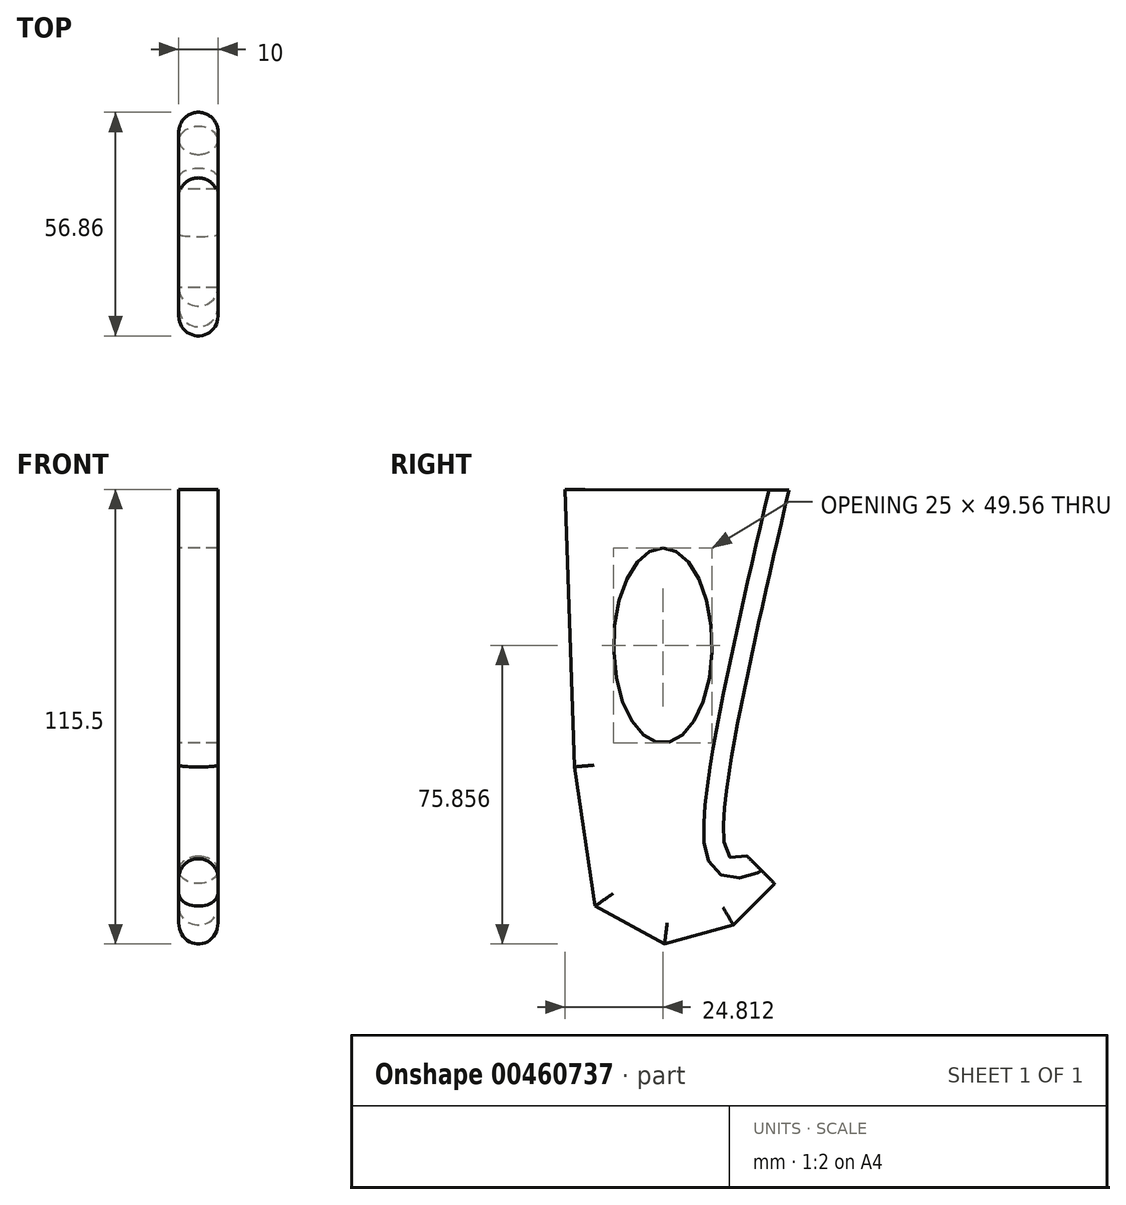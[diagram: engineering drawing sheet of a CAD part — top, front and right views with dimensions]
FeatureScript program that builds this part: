
annotation { "Feature Type Name" : "Feature", "Feature Type Description" : "" }
export const myFeature = defineFeature(function(context is Context, id is Id, definition is map)
    precondition{}
    {
        {
            var Q0;
            Q0=qCreatedBy(makeId("Top.planeOp"),FACE);
            var sketch = newSketch(context, id + "F0", { "sketchPlane" : qUnion([Q0])});
            skLineSegment(sketch, "E0.bottom", {"start": v(50, 50) * mm, "end": v(-50, 50) * mm});
            skLineSegment(sketch, "E0.top", {"start": v(50, -50) * mm, "end": v(-50, -50) * mm});
            skLineSegment(sketch, "E0.left", {"start": v(50, 50) * mm, "end": v(50, -50) * mm});
            skLineSegment(sketch, "E0.right", {"start": v(-50, 50) * mm, "end": v(-50, -50) * mm});
            skPoint(sketch, "E0.middle", {"position": v(0, 0) * mm});
            skSolve(sketch);
        }
        {
            var Q0;
            Q0=qCreatedBy(makeId("Right.planeOp"),FACE);
            var sketch = newSketch(context, id + "F1", { "sketchPlane" : qUnion([Q0])});
            skLineSegment(sketch, "E1", {"start": v(32.93, -92.93) * mm, "end": v(40, -100) * mm});
            skLineSegment(sketch, "E2", {"start": v(40, -100) * mm, "end": v(50, -100) * mm});
            skLineSegment(sketch, "E3", {"start": v(50, -100) * mm, "end": v(50, 0) * mm});
            skLineSegment(sketch, "E4", {"start": v(40, -100) * mm, "end": v(29.49, -110.51) * mm});
            skLineSegment(sketch, "E5", {"start": v(29.49, -110.51) * mm, "end": v(12.06, -115.35) * mm});
            skLineSegment(sketch, "E6", {"start": v(12.06, -115.35) * mm, "end": v(-5.63, -105.7) * mm});
            skLineSegment(sketch, "E7", {"start": v(-5.63, -105.7) * mm, "end": v(-10.9, -70.34) * mm});
            skLineSegment(sketch, "E8", {"start": v(-10.9, -70.34) * mm, "end": v(-13.2, 0.15) * mm});
            skFitSpline(sketch, "E9", {"points": [v(32.93, -92.93) * mm, v(28.21, -92.93) * mm, v(43.66, 0.05) * mm], "startDerivative": vector(-29.89, -10.4) * mm, "endDerivative": vector(37.17, 160.27) * mm});
            skLineSegment(sketch, "E10", {"start": v(43.66, 0.05) * mm, "end": v(-13.2, 0.15) * mm});
            skEllipse(sketch, "E11", {"center": v(11.61, -39.5) * mm, "majorRadius": 24.78 * mm, "minorRadius": 12.5 * mm, "majorAxis": v(0, 1)});
            skSolve(sketch);
        }
        {
            var Q0;
            Q0=makeQuery(id+"F1.imprint","IMPRINT",FACE,{"disambiguationData":[TD([[makeQuery(id+"F1.imprint","IMPRINT",EDGE,{"derivedFrom":sQuery(id+"F1.wireOp",EDGE,"E1")}),-1.0]])]});
            extrude(context, id + "F2", {"entities" : qUnion([Q0]), "endBound" : BoundingType.SYMMETRIC, "depth" : 10 * mm});
        }
        {
            var Q0;
            Q0=makeQuery(id+"F2.opExtrude","CAP_EDGE",EDGE,{"disambiguationData":[OSD([sQuery(id+"F1.wireOp",EDGE,"E9")])],"isStart":false});
            var Q1;
            Q1=makeQuery(id+"F2.opExtrude","CAP_EDGE",EDGE,{"disambiguationData":[OSD([sQuery(id+"F1.wireOp",EDGE,"E4")])],"isStart":false});
            var Q2;
            Q2=makeQuery(id+"F2.opExtrude","CAP_EDGE",EDGE,{"disambiguationData":[OSD([sQuery(id+"F1.wireOp",EDGE,"E5")])],"isStart":false});
            var Q3;
            Q3=makeQuery(id+"F2.opExtrude","CAP_EDGE",EDGE,{"disambiguationData":[OSD([sQuery(id+"F1.wireOp",EDGE,"E6")])],"isStart":false});
            var Q4;
            Q4=makeQuery(id+"F2.opExtrude","CAP_EDGE",EDGE,{"disambiguationData":[OSD([sQuery(id+"F1.wireOp",EDGE,"E7")])],"isStart":false});
            var Q5;
            Q5=makeQuery(id+"F2.opExtrude","CAP_EDGE",EDGE,{"disambiguationData":[OSD([sQuery(id+"F1.wireOp",EDGE,"E7")])],"isStart":false});
            var Q6;
            Q6=makeQuery(id+"F2.opExtrude","CAP_EDGE",EDGE,{"disambiguationData":[OSD([sQuery(id+"F1.wireOp",EDGE,"E8")])],"isStart":false});
            var Q7;
            Q7=makeQuery(id+"F2.opExtrude","CAP_EDGE",EDGE,{"disambiguationData":[OSD([sQuery(id+"F1.wireOp",EDGE,"E9")])],"isStart":true});
            var Q8;
            Q8=makeQuery(id+"F2.opExtrude","CAP_EDGE",EDGE,{"disambiguationData":[OSD([sQuery(id+"F1.wireOp",EDGE,"E4")])],"isStart":true});
            var Q9;
            Q9=makeQuery(id+"F2.opExtrude","CAP_EDGE",EDGE,{"disambiguationData":[OSD([sQuery(id+"F1.wireOp",EDGE,"E5")])],"isStart":true});
            var Q10;
            Q10=makeQuery(id+"F2.opExtrude","CAP_EDGE",EDGE,{"disambiguationData":[OSD([sQuery(id+"F1.wireOp",EDGE,"E6")])],"isStart":true});
            var Q11;
            Q11=makeQuery(id+"F2.opExtrude","CAP_EDGE",EDGE,{"disambiguationData":[OSD([sQuery(id+"F1.wireOp",EDGE,"E7")])],"isStart":true});
            var Q12;
            Q12=makeQuery(id+"F2.opExtrude","CAP_EDGE",EDGE,{"disambiguationData":[OSD([sQuery(id+"F1.wireOp",EDGE,"E8")])],"isStart":true});
            fillet(context, id + "F3", {"entities" : qUnion([Q0, Q1, Q2, Q3, Q4, Q5, Q6, Q7, Q8, Q9, Q10, Q11, Q12]), "radius" : 5 * mm, "tangentPropagation" : true, "allowEdgeOverflow" : false});
        }
    });
